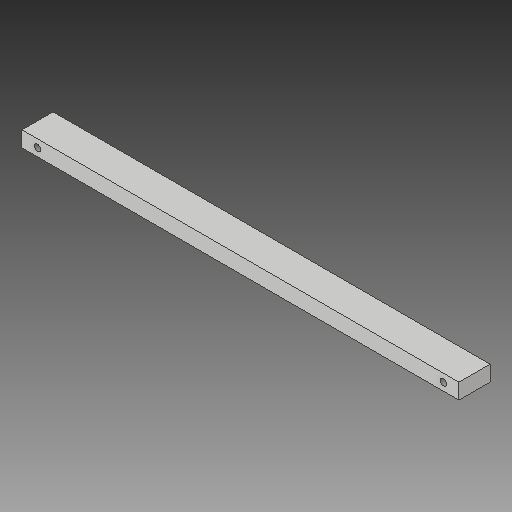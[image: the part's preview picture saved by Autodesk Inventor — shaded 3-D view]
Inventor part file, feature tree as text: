
AUTODESK INVENTOR PART (.ipt)
format: ipt  version: 2019 (Build 230136000, 136)  size: 106,496 bytes
history: native  units: in
note: dims shown in document units (in); Inventor stores cm internally (conversion verified against a paired STEP export)
features: sketch x2, extrude x1, hole x1
ambient origin geometry x8: Origin, YZ Plane, XZ Plane, XY Plane, X Axis, Y Axis, Z Axis, Center Point
bodies: Solid1 (feature_tree)
feature tree (4):
  extrude  "Extrusion1"  Depth=0.25in
  hole  "Hole1"  [1 undecoded]
  sketch  "Sketch1"  dims[d0=7.016in d1=0.25in]
  sketch  "Sketch2"  dims[d2=0.5in d3=0.0in d4=0.25in d5=0.25in d6=0.14in d7=0.14in d10=0.104in d11=0.5in d12=0.375in d13=0.25in d14=0.5635in d15=0.5in d16=0.8108in]
note: 1 required parameter value undecoded (feature->parameter linkage not recoverable at this tier; creation-order binding heuristic only, values carry confidence <= 0.55)
